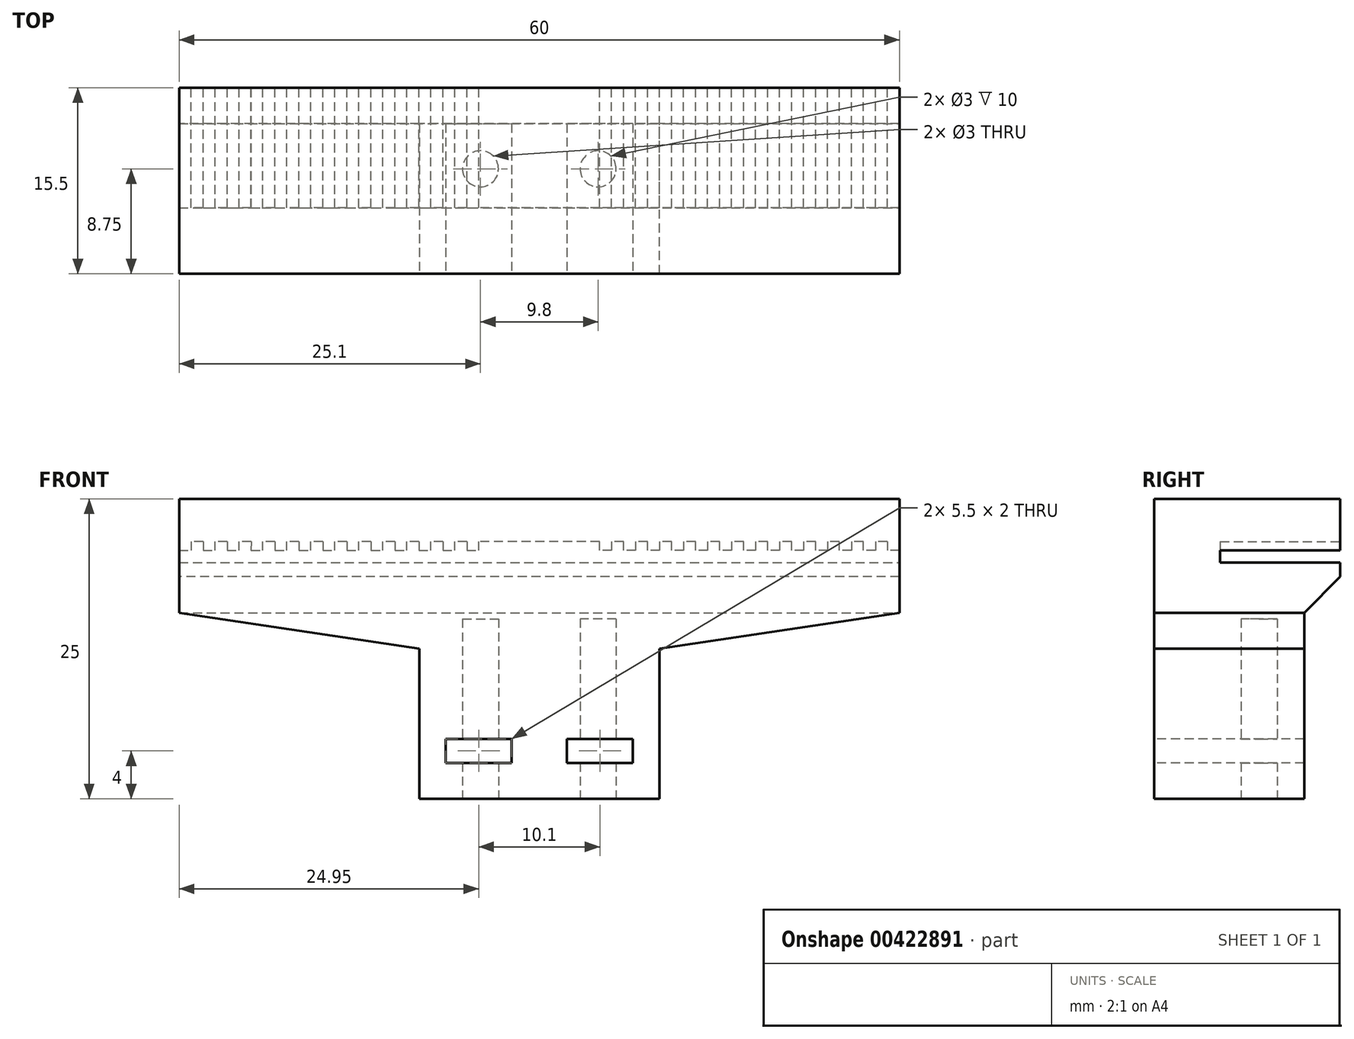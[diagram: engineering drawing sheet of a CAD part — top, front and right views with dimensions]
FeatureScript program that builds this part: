
annotation { "Feature Type Name" : "Feature", "Feature Type Description" : "" }
export const myFeature = defineFeature(function(context is Context, id is Id, definition is map)
    precondition{}
    {
        {
            var Q0;
            Q0=qCreatedBy(makeId("Top.planeOp"),FACE);
            var sketch = newSketch(context, id + "F0", { "sketchPlane" : qUnion([Q0])});
            skLineSegment(sketch, "E0.bottom", {"start": v(10, 3.75) * mm, "end": v(-10, 3.75) * mm});
            skLineSegment(sketch, "E0.top", {"start": v(10, -3.75) * mm, "end": v(-10, -3.75) * mm});
            skLineSegment(sketch, "E0.left", {"start": v(10, 3.75) * mm, "end": v(10, -3.75) * mm});
            skLineSegment(sketch, "E0.right", {"start": v(-10, 3.75) * mm, "end": v(-10, -3.75) * mm});
            skPoint(sketch, "E0.middle", {"position": v(0, 0) * mm});
            skLineSegment(sketch, "E1", {"start": v(0, 0) * mm, "end": v(-4.9, 0) * mm, "construction": true});
            skLineSegment(sketch, "E2", {"start": v(0, 0) * mm, "end": v(4.9, 0) * mm, "construction": true});
            skCircle(sketch, "E3", {"center": v(-4.9, 0) * mm, "radius": 1.5 * mm});
            skCircle(sketch, "E4", {"center": v(4.9, 0) * mm, "radius": 1.5 * mm});
            skSolve(sketch);
        }
        {
            var Q0;
            Q0=makeQuery(id+"F0.imprint","IMPRINT",FACE,{"disambiguationData":[TD([[makeQuery(id+"F0.imprint","IMPRINT",EDGE,{"derivedFrom":sQuery(id+"F0.wireOp",EDGE,"E0.bottom")}),1.0]])]});
            extrude(context, id + "F1", {"entities" : qUnion([Q0]), "depth" : 25 * mm});
        }
        {
            var Q0;
            Q0=makeQuery(id+"F1.opExtrude","CAP_FACE",FACE,{"disambiguationData":[OSD([sQuery(id+"F0.wireOp",EDGE,"E0.bottom"),sQuery(id+"F0.wireOp",EDGE,"E0.top"),sQuery(id+"F0.wireOp",EDGE,"E0.left"),sQuery(id+"F0.wireOp",EDGE,"E0.right"),sQuery(id+"F0.wireOp",EDGE,"E3"),sQuery(id+"F0.wireOp",EDGE,"E4")])],"isStart":false});
            var sketch = newSketch(context, id + "F2", { "sketchPlane" : qUnion([Q0])});
            skLineSegment(sketch, "E5.bottom", {"start": v(-10, -3.75) * mm, "end": v(10, -3.75) * mm});
            skLineSegment(sketch, "E5.top", {"start": v(-10, 3.75) * mm, "end": v(10, 3.75) * mm});
            skLineSegment(sketch, "E5.left", {"start": v(-10, -3.75) * mm, "end": v(-10, 3.75) * mm});
            skLineSegment(sketch, "E5.right", {"start": v(10, -3.75) * mm, "end": v(10, 3.75) * mm});
            skSolve(sketch);
        }
        {
            var Q0;
            Q0 = qSketchRegion(id + "F2", true);
            extrude(context, id + "F3", {"entities" : qUnion([Q0]), "operationType" : NewBodyOperationType.ADD, "oppositeDirection" : true, "depth" : 10 * mm});
        }
        {
            var Q0;
            Q0=makeQuery(id+"F1.opExtrude","SWEPT_FACE",FACE,{"disambiguationData":[OSD([sQuery(id+"F0.wireOp",EDGE,"E0.top")])]});
            var sketch = newSketch(context, id + "F4", { "sketchPlane" : qUnion([Q0])});
            skLineSegment(sketch, "E6", {"start": v(0, 0) * mm, "end": v(0, 25) * mm, "construction": true});
            skLineSegment(sketch, "E7", {"start": v(0, 0) * mm, "end": v(0, 3) * mm});
            skLineSegment(sketch, "E8", {"start": v(0, 3) * mm, "end": v(-7.8, 3) * mm, "construction": true});
            skLineSegment(sketch, "E9", {"start": v(0, 3) * mm, "end": v(7.8, 3) * mm, "construction": true});
            skLineSegment(sketch, "E10", {"start": v(-7.8, 3) * mm, "end": v(-7.8, 5) * mm, "construction": true});
            skLineSegment(sketch, "E11", {"start": v(-7.8, 5) * mm, "end": v(-2.3, 5) * mm, "construction": true});
            skLineSegment(sketch, "E12", {"start": v(-2.3, 5) * mm, "end": v(-2.3, 3) * mm, "construction": true});
            skLineSegment(sketch, "E13", {"start": v(7.8, 3) * mm, "end": v(7.8, 5) * mm, "construction": true});
            skLineSegment(sketch, "E14", {"start": v(7.8, 5) * mm, "end": v(2.3, 5) * mm, "construction": true});
            skLineSegment(sketch, "E15", {"start": v(2.3, 5) * mm, "end": v(2.3, 3) * mm, "construction": true});
            skLineSegment(sketch, "E16", {"start": v(-7.8, 5) * mm, "end": v(-2.3, 5) * mm});
            skLineSegment(sketch, "E17", {"start": v(-2.3, 5) * mm, "end": v(-2.3, 3) * mm});
            skLineSegment(sketch, "E18", {"start": v(-2.3, 3) * mm, "end": v(-7.8, 3) * mm});
            skLineSegment(sketch, "E19", {"start": v(-7.8, 3) * mm, "end": v(-7.8, 5) * mm});
            skLineSegment(sketch, "E20", {"start": v(2.3, 3) * mm, "end": v(7.8, 3) * mm});
            skLineSegment(sketch, "E21", {"start": v(7.8, 3) * mm, "end": v(7.8, 5) * mm});
            skLineSegment(sketch, "E22", {"start": v(7.8, 5) * mm, "end": v(2.3, 5) * mm});
            skLineSegment(sketch, "E23", {"start": v(2.3, 5) * mm, "end": v(2.3, 3) * mm});
            skSolve(sketch);
        }
        {
            var Q0;
            Q0=makeQuery(id+"F4.imprint","IMPRINT",FACE,{"disambiguationData":[TD([[makeQuery(id+"F4.imprint","IMPRINT",EDGE,{"derivedFrom":sQuery(id+"F4.wireOp",EDGE,"E16")}),-1.0]])]});
            var Q1;
            Q1=makeQuery(id+"F4.imprint","IMPRINT",FACE,{"disambiguationData":[TD([[makeQuery(id+"F4.imprint","IMPRINT",EDGE,{"derivedFrom":sQuery(id+"F4.wireOp",EDGE,"E20")}),1.0]])]});
            extrude(context, id + "F5", {"entities" : qUnion([Q0, Q1]), "operationType" : NewBodyOperationType.REMOVE, "oppositeDirection" : true, "depth" : 7.5 * mm});
        }
        {
            var Q0;
            Q0=makeQuery(id+"F1.opExtrude","SWEPT_FACE",FACE,{"disambiguationData":[OSD([sQuery(id+"F0.wireOp",EDGE,"E0.right")])]});
            var sketch = newSketch(context, id + "F6", { "sketchPlane" : qUnion([Q0])});
            skLineSegment(sketch, "E24", {"start": v(-3.75, 25) * mm, "end": v(-3.75, 12.5) * mm});
            skLineSegment(sketch, "E25", {"start": v(-3.75, 12.5) * mm, "end": v(3.75, 12.5) * mm});
            skLineSegment(sketch, "E26", {"start": v(3.75, 12.5) * mm, "end": v(3.75, 25) * mm});
            skLineSegment(sketch, "E27", {"start": v(3.75, 25) * mm, "end": v(-3.75, 25) * mm});
            skSolve(sketch);
        }
        {
            var Q0;
            Q0=makeQuery(id+"F6.imprint","IMPRINT",FACE,{"disambiguationData":[TD([[makeQuery(id+"F6.imprint","IMPRINT",EDGE,{"derivedFrom":sQuery(id+"F6.wireOp",EDGE,"E24")}),1.0]])]});
            extrude(context, id + "F7", {"entities" : qUnion([Q0]), "operationType" : NewBodyOperationType.ADD, "depth" : 20 * mm});
        }
        {
            var Q0;
            Q0=makeQuery(id+"F1.opExtrude","SWEPT_FACE",FACE,{"disambiguationData":[OSD([sQuery(id+"F0.wireOp",EDGE,"E0.left")])]});
            var sketch = newSketch(context, id + "F8", { "sketchPlane" : qUnion([Q0])});
            skLineSegment(sketch, "E28", {"start": v(3.75, 25) * mm, "end": v(-3.75, 25) * mm});
            skLineSegment(sketch, "E29", {"start": v(-3.75, 25) * mm, "end": v(-3.75, 12.5) * mm});
            skLineSegment(sketch, "E30", {"start": v(-3.75, 12.5) * mm, "end": v(3.75, 12.5) * mm});
            skLineSegment(sketch, "E31", {"start": v(3.75, 12.5) * mm, "end": v(3.75, 25) * mm});
            skSolve(sketch);
        }
        {
            var Q0;
            Q0=makeQuery(id+"F8.imprint","IMPRINT",FACE,{"disambiguationData":[TD([[makeQuery(id+"F8.imprint","IMPRINT",EDGE,{"derivedFrom":sQuery(id+"F8.wireOp",EDGE,"E28")}),1.0]])]});
            extrude(context, id + "F9", {"entities" : qUnion([Q0]), "operationType" : NewBodyOperationType.ADD, "depth" : 20 * mm});
        }
        {
            var Q0;
            Q0=makeQuery(id+"F7.opExtrude","CAP_EDGE",EDGE,{"disambiguationData":[OSD([sQuery(id+"F6.wireOp",EDGE,"E25")])],"isStart":false});
            var Q1;
            Q1=makeQuery(id+"F9.opExtrude","CAP_EDGE",EDGE,{"disambiguationData":[OSD([sQuery(id+"F8.wireOp",EDGE,"E30")])],"isStart":false});
            chamfer(context, id + "F10", {"entities" : qUnion([Q0, Q1]), "chamferType" : ChamferType.TWO_OFFSETS, "width1" : 3 * mm, "oppositeDirection" : false, "width2" : 20 * mm, "tangentPropagation" : true});
        }
        {
            var Q0;
            Q0=makeQuery(id+"F9.boolean.opBoolean","MERGE",FACE,{"derivedFrom":[makeQuery(id+"F7.boolean.opBoolean","MERGE",FACE,{"derivedFrom":[makeQuery(id+"F1.opExtrude","SWEPT_FACE",FACE,{"disambiguationData":[OSD([sQuery(id+"F0.wireOp",EDGE,"E0.bottom")])]}),makeQuery(id+"F7.opExtrude","SWEPT_FACE",FACE,{"disambiguationData":[OSD([sQuery(id+"F6.wireOp",EDGE,"E24")])]})]}),makeQuery(id+"F9.opExtrude","SWEPT_FACE",FACE,{"disambiguationData":[OSD([sQuery(id+"F8.wireOp",EDGE,"E31")])]})]});
            var sketch = newSketch(context, id + "F11", { "sketchPlane" : qUnion([Q0])});
            skLineSegment(sketch, "E32", {"start": v(30, 15.5) * mm, "end": v(-30, 15.5) * mm});
            skSolve(sketch);
        }
        {
            var Q0;
            Q0=makeQuery(id+"F11.imprint","IMPRINT",FACE,{"disambiguationData":[TD([[makeQuery(id+"F11.imprint","IMPRINT",EDGE,{"derivedFrom":sQuery(id+"F11.wireOp",EDGE,"E32")}),-1.0]])]});
            extrude(context, id + "F12", {"entities" : qUnion([Q0]), "operationType" : NewBodyOperationType.ADD, "depth" : 3 * mm});
        }
        {
            var Q0;
            Q0=makeQuery(id+"F9.boolean.opBoolean","MERGE",FACE,{"derivedFrom":[makeQuery(id+"F7.boolean.opBoolean","MERGE",FACE,{"derivedFrom":[makeQuery(id+"F1.opExtrude","SWEPT_FACE",FACE,{"disambiguationData":[OSD([sQuery(id+"F0.wireOp",EDGE,"E0.top")])]}),makeQuery(id+"F7.opExtrude","SWEPT_FACE",FACE,{"disambiguationData":[OSD([sQuery(id+"F6.wireOp",EDGE,"E26")])]})]}),makeQuery(id+"F9.opExtrude","SWEPT_FACE",FACE,{"disambiguationData":[OSD([sQuery(id+"F8.wireOp",EDGE,"E29")])]})]});
            var sketch = newSketch(context, id + "F13", { "sketchPlane" : qUnion([Q0])});
            skLineSegment(sketch, "E33", {"start": v(30, 15.5) * mm, "end": v(-30, 15.5) * mm});
            skSolve(sketch);
        }
        {
            var Q0;
            Q0=makeQuery(id+"F12.opExtrude","CAP_EDGE",EDGE,{"disambiguationData":[OSD([sQuery(id+"F11.wireOp",EDGE,"E32")])],"isStart":false});
            var Q1;
            Q1=makeQuery(id+"Fa86QrGP9sfaCBA_1.opExtrude","CAP_EDGE",EDGE,{"disambiguationData":[OSD([sQuery(id+"F13.wireOp",EDGE,"E33")])],"isStart":false});
            chamfer(context, id + "F14", {"entities" : qUnion([Q0, Q1]), "width" : 3 * mm, "tangentPropagation" : true});
        }
        {
            var Q0;
            Q0=makeQuery(id+"F12.opExtrude","CAP_FACE",FACE,{"disambiguationData":[OSD([sQuery(id+"F0.wireOp",EDGE,"E0.bottom"),sQuery(id+"F6.wireOp",EDGE,"E24"),sQuery(id+"F6.wireOp",EDGE,"E27"),sQuery(id+"F8.wireOp",EDGE,"E28"),sQuery(id+"F8.wireOp",EDGE,"E31"),sQuery(id+"F11.wireOp",EDGE,"E32")])],"isStart":false});
            var sketch = newSketch(context, id + "F15", { "sketchPlane" : qUnion([Q0])});
            skLineSegment(sketch, "E34", {"start": v(30, 21.75) * mm, "end": v(-30, 21.75) * mm});
            skLineSegment(sketch, "E35", {"start": v(-30, 21.75) * mm, "end": v(-30, 21.45) * mm});
            skLineSegment(sketch, "E36", {"start": v(-30, 21.45) * mm, "end": v(30, 21.45) * mm});
            skLineSegment(sketch, "E37", {"start": v(30, 21.45) * mm, "end": v(30, 21.75) * mm});
            skLineSegment(sketch, "E38.bottom", {"start": v(30, 21.45) * mm, "end": v(29, 21.45) * mm});
            skLineSegment(sketch, "E38.top", {"start": v(30, 20.7) * mm, "end": v(29, 20.7) * mm});
            skLineSegment(sketch, "E38.left", {"start": v(30, 21.45) * mm, "end": v(30, 20.7) * mm});
            skLineSegment(sketch, "E38.right", {"start": v(29, 21.45) * mm, "end": v(29, 20.7) * mm});
            skLineSegment(sketch, "E39", {"start": v(29, 21.45) * mm, "end": v(28, 21.45) * mm});
            skLineSegment(sketch, "E40", {"start": v(28, 21.45) * mm, "end": v(28, 20.7) * mm});
            skLineSegment(sketch, "E41", {"start": v(28, 20.7) * mm, "end": v(27, 20.7) * mm});
            skLineSegment(sketch, "E42", {"start": v(27, 20.7) * mm, "end": v(27, 21.45) * mm});
            skLineSegment(sketch, "E43", {"start": v(27, 21.45) * mm, "end": v(26, 21.45) * mm});
            skLineSegment(sketch, "E44", {"start": v(26, 21.45) * mm, "end": v(26, 20.7) * mm});
            skLineSegment(sketch, "E45", {"start": v(26, 20.7) * mm, "end": v(25, 20.7) * mm});
            skLineSegment(sketch, "E46", {"start": v(25, 20.7) * mm, "end": v(25, 21.45) * mm});
            skLineSegment(sketch, "E47", {"start": v(25, 21.45) * mm, "end": v(24, 21.45) * mm});
            skLineSegment(sketch, "E48", {"start": v(24, 21.45) * mm, "end": v(24.03, 20.7) * mm});
            skLineSegment(sketch, "E49", {"start": v(24.03, 20.7) * mm, "end": v(23.03, 20.7) * mm});
            skLineSegment(sketch, "E50", {"start": v(23.03, 20.7) * mm, "end": v(23.03, 21.45) * mm});
            skLineSegment(sketch, "E51", {"start": v(23.03, 21.45) * mm, "end": v(22.03, 21.45) * mm});
            skLineSegment(sketch, "E52", {"start": v(22.03, 21.45) * mm, "end": v(22.03, 20.7) * mm});
            skLineSegment(sketch, "E53", {"start": v(22.03, 20.7) * mm, "end": v(21.03, 20.7) * mm});
            skLineSegment(sketch, "E54", {"start": v(21.03, 20.7) * mm, "end": v(21.03, 21.45) * mm});
            skLineSegment(sketch, "E55", {"start": v(21.03, 21.45) * mm, "end": v(20.03, 21.45) * mm});
            skLineSegment(sketch, "E56", {"start": v(20.03, 21.45) * mm, "end": v(20.03, 20.7) * mm});
            skLineSegment(sketch, "E57", {"start": v(20.03, 20.7) * mm, "end": v(19.03, 20.7) * mm});
            skLineSegment(sketch, "E58", {"start": v(19.03, 20.7) * mm, "end": v(19.03, 21.45) * mm});
            skLineSegment(sketch, "E59", {"start": v(19.03, 21.45) * mm, "end": v(18.03, 21.45) * mm});
            skLineSegment(sketch, "E60", {"start": v(18.03, 21.45) * mm, "end": v(18.03, 20.7) * mm});
            skLineSegment(sketch, "E61", {"start": v(18.03, 20.7) * mm, "end": v(17.03, 20.7) * mm});
            skLineSegment(sketch, "E62", {"start": v(17.03, 20.7) * mm, "end": v(17.03, 21.45) * mm});
            skLineSegment(sketch, "E63", {"start": v(17.03, 21.45) * mm, "end": v(16.03, 21.45) * mm});
            skLineSegment(sketch, "E64", {"start": v(16.03, 21.45) * mm, "end": v(16.03, 20.7) * mm});
            skLineSegment(sketch, "E65", {"start": v(16.03, 20.7) * mm, "end": v(15.03, 20.7) * mm});
            skLineSegment(sketch, "E66", {"start": v(15.03, 20.7) * mm, "end": v(15.03, 21.45) * mm});
            skLineSegment(sketch, "E67", {"start": v(15.03, 21.45) * mm, "end": v(14.03, 21.45) * mm});
            skLineSegment(sketch, "E68", {"start": v(14.03, 21.45) * mm, "end": v(14.03, 20.7) * mm});
            skLineSegment(sketch, "E69", {"start": v(14.03, 20.7) * mm, "end": v(13.03, 20.7) * mm});
            skLineSegment(sketch, "E70", {"start": v(13.03, 20.7) * mm, "end": v(13.03, 21.45) * mm});
            skLineSegment(sketch, "E71", {"start": v(13.03, 21.45) * mm, "end": v(12.03, 21.45) * mm});
            skLineSegment(sketch, "E72", {"start": v(12.03, 21.45) * mm, "end": v(12.03, 20.7) * mm});
            skLineSegment(sketch, "E73", {"start": v(12.03, 20.7) * mm, "end": v(11.03, 20.7) * mm});
            skLineSegment(sketch, "E74", {"start": v(11.03, 20.7) * mm, "end": v(11.03, 21.45) * mm});
            skLineSegment(sketch, "E75", {"start": v(11.03, 21.45) * mm, "end": v(10.03, 21.45) * mm});
            skLineSegment(sketch, "E76", {"start": v(10.03, 21.45) * mm, "end": v(10.03, 20.7) * mm});
            skLineSegment(sketch, "E77", {"start": v(10.03, 20.7) * mm, "end": v(9.03, 20.7) * mm});
            skLineSegment(sketch, "E78", {"start": v(9.03, 20.7) * mm, "end": v(9.03, 21.45) * mm});
            skLineSegment(sketch, "E79", {"start": v(9.03, 21.45) * mm, "end": v(8.03, 21.45) * mm});
            skLineSegment(sketch, "E80", {"start": v(8.03, 21.45) * mm, "end": v(8.03, 20.7) * mm});
            skLineSegment(sketch, "E81", {"start": v(8.03, 20.7) * mm, "end": v(7.03, 20.7) * mm});
            skLineSegment(sketch, "E82", {"start": v(7.03, 20.7) * mm, "end": v(7.03, 21.45) * mm});
            skLineSegment(sketch, "E83", {"start": v(7.03, 21.45) * mm, "end": v(6.03, 21.45) * mm});
            skLineSegment(sketch, "E84", {"start": v(6.03, 21.45) * mm, "end": v(6.03, 20.7) * mm});
            skLineSegment(sketch, "E85", {"start": v(6.03, 20.7) * mm, "end": v(5.03, 20.7) * mm});
            skLineSegment(sketch, "E86", {"start": v(5.03, 20.7) * mm, "end": v(5.03, 21.45) * mm});
            skLineSegment(sketch, "E87", {"start": v(5.03, 21.45) * mm, "end": v(4.03, 21.45) * mm});
            skLineSegment(sketch, "E88.MirrorCS", {"start": v(-30, 21.45) * mm, "end": v(-30, 20.7) * mm});
            skLineSegment(sketch, "E89.MirrorCS", {"start": v(-30, 20.7) * mm, "end": v(-29, 20.7) * mm});
            skLineSegment(sketch, "E90.MirrorCS", {"start": v(-29, 21.45) * mm, "end": v(-29, 20.7) * mm});
            skLineSegment(sketch, "E91.MirrorCS", {"start": v(-29, 21.45) * mm, "end": v(-28, 21.45) * mm});
            skLineSegment(sketch, "E92.MirrorCS", {"start": v(-28, 21.45) * mm, "end": v(-28, 20.7) * mm});
            skLineSegment(sketch, "E93.MirrorCS", {"start": v(-28, 20.7) * mm, "end": v(-27, 20.7) * mm});
            skLineSegment(sketch, "E94.MirrorCS", {"start": v(-27, 20.7) * mm, "end": v(-27, 21.45) * mm});
            skLineSegment(sketch, "E95.MirrorCS", {"start": v(-27, 21.45) * mm, "end": v(-26, 21.45) * mm});
            skLineSegment(sketch, "E96.MirrorCS", {"start": v(-26, 21.45) * mm, "end": v(-26, 20.7) * mm});
            skLineSegment(sketch, "E97.MirrorCS", {"start": v(-26, 20.7) * mm, "end": v(-25, 20.7) * mm});
            skLineSegment(sketch, "E98.MirrorCS", {"start": v(-25, 20.7) * mm, "end": v(-25, 21.45) * mm});
            skLineSegment(sketch, "E99.MirrorCS", {"start": v(-24, 21.45) * mm, "end": v(-24.03, 20.7) * mm});
            skLineSegment(sketch, "E100.MirrorCS", {"start": v(30, 21.45) * mm, "end": v(-30, 21.45) * mm});
            skLineSegment(sketch, "E101.MirrorCS", {"start": v(-24.03, 20.7) * mm, "end": v(-23.03, 20.7) * mm});
            skLineSegment(sketch, "E102.MirrorCS", {"start": v(-23.03, 20.7) * mm, "end": v(-23.03, 21.45) * mm});
            skLineSegment(sketch, "E103.MirrorCS", {"start": v(-22.03, 21.45) * mm, "end": v(-22.03, 20.7) * mm});
            skLineSegment(sketch, "E104.MirrorCS", {"start": v(-22.03, 20.7) * mm, "end": v(-21.03, 20.7) * mm});
            skLineSegment(sketch, "E105.MirrorCS", {"start": v(-21.03, 20.7) * mm, "end": v(-21.03, 21.45) * mm});
            skLineSegment(sketch, "E106.MirrorCS", {"start": v(-20.03, 21.45) * mm, "end": v(-20.03, 20.7) * mm});
            skLineSegment(sketch, "E107.MirrorCS", {"start": v(-20.03, 20.7) * mm, "end": v(-19.03, 20.7) * mm});
            skLineSegment(sketch, "E108.MirrorCS", {"start": v(-19.03, 20.7) * mm, "end": v(-19.03, 21.45) * mm});
            skLineSegment(sketch, "E109.MirrorCS", {"start": v(-18.03, 21.45) * mm, "end": v(-18.03, 20.7) * mm});
            skLineSegment(sketch, "E110.MirrorCS", {"start": v(-18.03, 20.7) * mm, "end": v(-17.03, 20.7) * mm});
            skLineSegment(sketch, "E111.MirrorCS", {"start": v(-17.03, 20.7) * mm, "end": v(-17.03, 21.45) * mm});
            skLineSegment(sketch, "E112.MirrorCS", {"start": v(-16.03, 21.45) * mm, "end": v(-16.03, 20.7) * mm});
            skLineSegment(sketch, "E113.MirrorCS", {"start": v(-16.03, 20.7) * mm, "end": v(-15.03, 20.7) * mm});
            skLineSegment(sketch, "E114.MirrorCS", {"start": v(-15.03, 20.7) * mm, "end": v(-15.03, 21.45) * mm});
            skLineSegment(sketch, "E115.MirrorCS", {"start": v(-14.03, 21.45) * mm, "end": v(-14.03, 20.7) * mm});
            skLineSegment(sketch, "E116.MirrorCS", {"start": v(-13.03, 20.7) * mm, "end": v(-13.03, 21.45) * mm});
            skLineSegment(sketch, "E117.MirrorCS", {"start": v(-12.03, 21.45) * mm, "end": v(-12.03, 20.7) * mm});
            skLineSegment(sketch, "E118.MirrorCS", {"start": v(-12.03, 20.7) * mm, "end": v(-11.03, 20.7) * mm});
            skLineSegment(sketch, "E119.MirrorCS", {"start": v(-11.03, 20.7) * mm, "end": v(-11.03, 21.45) * mm});
            skLineSegment(sketch, "E120.MirrorCS", {"start": v(-10.03, 21.45) * mm, "end": v(-10.03, 20.7) * mm});
            skLineSegment(sketch, "E121.MirrorCS", {"start": v(-10.03, 20.7) * mm, "end": v(-9.03, 20.7) * mm});
            skLineSegment(sketch, "E122.MirrorCS", {"start": v(-9.03, 20.7) * mm, "end": v(-9.03, 21.45) * mm});
            skLineSegment(sketch, "E123.MirrorCS", {"start": v(-8.03, 21.45) * mm, "end": v(-8.03, 20.7) * mm});
            skLineSegment(sketch, "E124.MirrorCS", {"start": v(-8.03, 20.7) * mm, "end": v(-7.03, 20.7) * mm});
            skLineSegment(sketch, "E125.MirrorCS", {"start": v(-7.03, 20.7) * mm, "end": v(-7.03, 21.45) * mm});
            skLineSegment(sketch, "E126.MirrorCS", {"start": v(-6.03, 21.45) * mm, "end": v(-6.03, 20.7) * mm});
            skLineSegment(sketch, "E127.MirrorCS", {"start": v(-6.03, 20.7) * mm, "end": v(-5.03, 20.7) * mm});
            skLineSegment(sketch, "E128.MirrorCS", {"start": v(-5.03, 20.7) * mm, "end": v(-5.03, 21.45) * mm});
            skLineSegment(sketch, "E129.MirrorCS", {"start": v(-5.03, 21.45) * mm, "end": v(-4.03, 21.45) * mm});
            skLineSegment(sketch, "E130", {"start": v(-14.03, 20.7) * mm, "end": v(-13.03, 20.7) * mm});
            skLineSegment(sketch, "E131", {"start": v(30, 20.7) * mm, "end": v(30, 19.7) * mm});
            skLineSegment(sketch, "E132", {"start": v(30, 19.7) * mm, "end": v(-30, 19.7) * mm});
            skLineSegment(sketch, "E133", {"start": v(-30, 19.7) * mm, "end": v(-30, 20.7) * mm});
            skSolve(sketch);
        }
        {
            var Q0;
            {var subQ52=sQuery(id+"F15.wireOp",EDGE,"E38.top");Q0=makeQuery(id+"F15.imprint","IMPRINT",FACE,{"disambiguationData":[TD([[makeQuery(id+"F15.imprint","IMPRINT",EDGE,{"derivedFrom":subQ52}),1.0]])]});}
            extrude(context, id + "F16", {"entities" : qUnion([Q0]), "operationType" : NewBodyOperationType.REMOVE, "oppositeDirection" : true, "depth" : 10 * mm});
        }
        {
            var Q0;
            Q0=makeQuery(id+"F13.imprint","IMPRINT",FACE,{"disambiguationData":[TD([[makeQuery(id+"F13.imprint","IMPRINT",EDGE,{"derivedFrom":sQuery(id+"F13.wireOp",EDGE,"E33")}),-1.0]])]});
            var Q1;
            Q1=makeQuery(id+"F13.imprint","IMPRINT",FACE,{"disambiguationData":[TD([[makeQuery(id+"F13.imprint","IMPRINT",EDGE,{"derivedFrom":sQuery(id+"F13.wireOp",EDGE,"E33")}),1.0]])]});
            extrude(context, id + "F17", {"entities" : qUnion([Q0, Q1]), "operationType" : NewBodyOperationType.ADD, "depth" : 5 * mm});
        }
    });
